# Revit family: FU_Chair_Sandler_Woodlook 2-9
name_source: partatom
category: Furniture
units: mm (PartAtom-declared; Revit-internal decimal feet)

## family parameters
Always vertical = Yes
Cut with Voids When Loaded = No
OmniClass Number = 23.40.20.00
OmniClass Title = General Furniture and Specialties
Room Calculation Point = No
Shared = No
Work Plane-Based = No

## types (3) — shared parameters
Depth = 585 mm  [stored 1.91929 ft]
Height = 833 mm  [stored 2.73294 ft]
Manufacturer = Sandler
URL = https://www.sandlerseating.com
Width = 510 mm  [stored 1.67323 ft]
zero-valued in all types: Default Elevation

## per-type parameters (varying)
| type | Arm Width | Description | Grab Handle | Stretchers | Upholstery | Woodlook |
| Woodlook 2.9 | 600 mm | Woodlook armchair with frame manufactured entirely from aluminum but with realistic appearance of wood. Highly durable and scratch resistant. Stacks 5. | No | Yes | Fabric - Mainline Flax - Upminster MLF20 | Woodlook - 24A Walnut |
| Woodlook 2.9NS | 560 mm  [stored 1.83727 ft] | Woodlook armchair with stretchers, frame manufactured entirely from aluminum but with realistic appearance of wood.
Highly durable and scratch resistant. Non-Stacking. | No | Yes | Fabric - Mainline Flax - Upminster MLF20 | Woodlook - 21A Teak |
| Woodlook 2.9GH | 600 mm | Woodlook armchair with frame manufactured entirely from aluminum but with realistic appearance of wood. Highly durable and scratch resistant. Stacks 5. With grip handle. | Yes | No | Woodlook - Vinyl - Slate | Woodlook - 20A Natural Beech |

note: column(s) folded — value = type name in every type: Model

note: [stored X ft] marks values corroborated as IEEE doubles in the binary element streams (Revit-internal decimal feet)

## geometry (parser evidence)
native form markers: Sweep x6
no freeform markers — native parametric forms only
